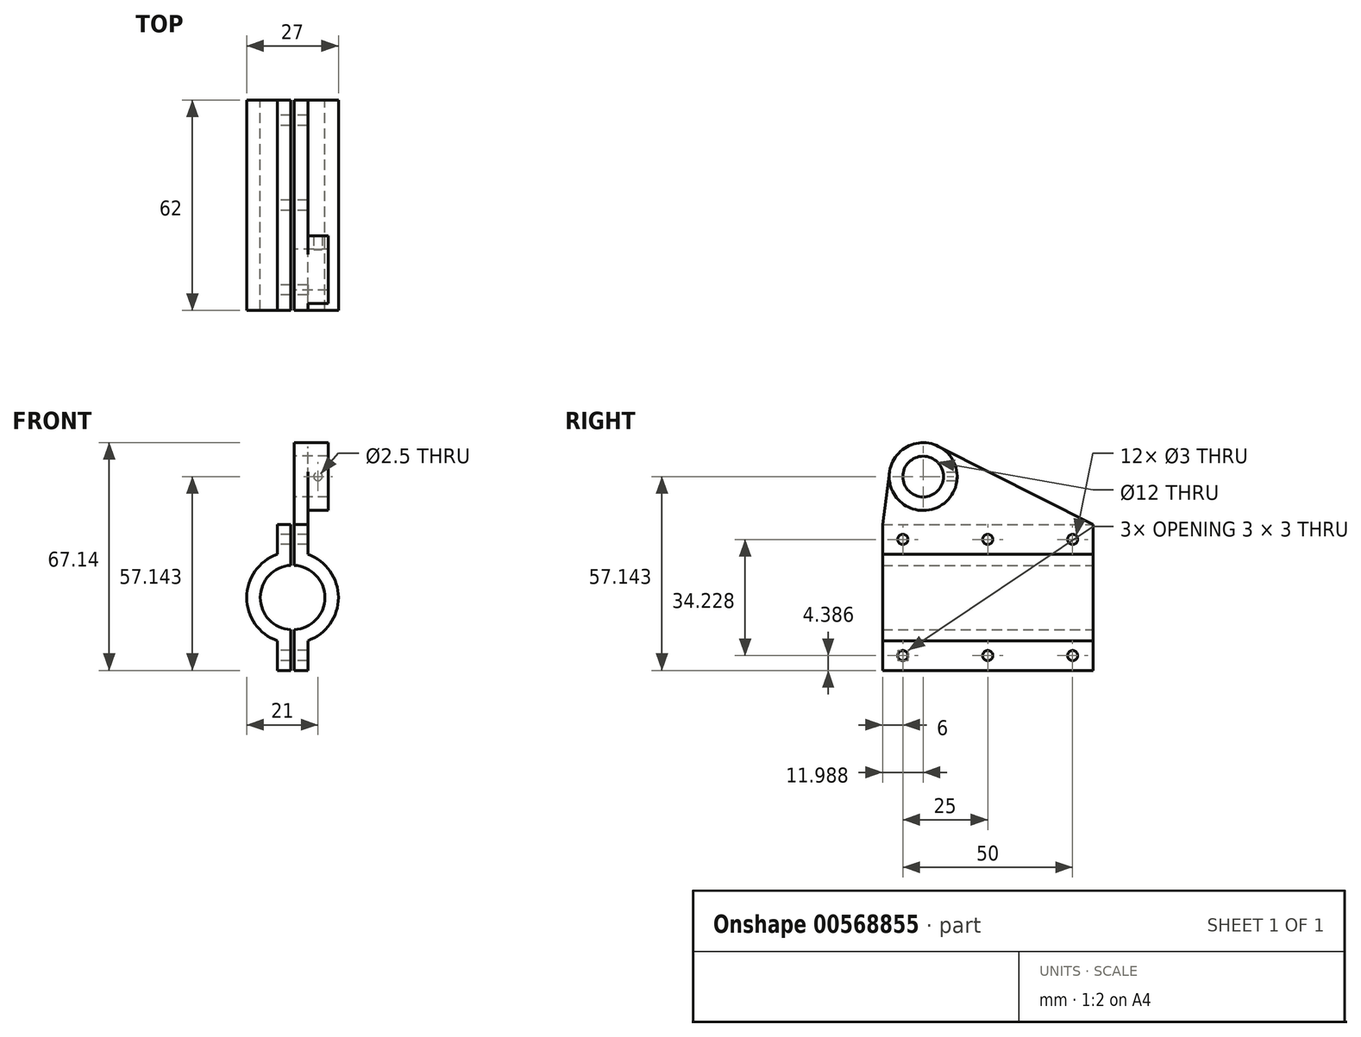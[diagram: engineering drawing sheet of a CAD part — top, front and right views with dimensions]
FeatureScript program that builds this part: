
annotation { "Feature Type Name" : "Feature", "Feature Type Description" : "" }
export const myFeature = defineFeature(function(context is Context, id is Id, definition is map)
    precondition{}
    {
        {
            var Q0;
            Q0=qCreatedBy(makeId("Front.planeOp"),FACE);
            var sketch = newSketch(context, id + "F0", { "sketchPlane" : qUnion([Q0])});
            skArc(sketch, "E0", {"start": v(-0.5, 9.49) * mm, "mid": v(-9.5, 0) * mm, "end": v(-0.5, -9.49) * mm});
            skArc(sketch, "E1", {"start": v(-4.5, 12.73) * mm, "mid": v(-13.5, 0) * mm, "end": v(-4.5, -12.73) * mm});
            skLineSegment(sketch, "E2", {"start": v(0, 28.47) * mm, "end": v(0, -33.23) * mm, "construction": true});
            skCircle(sketch, "E3", {"center": v(0, 0) * mm, "radius": 6 * mm, "construction": true});
            skLineSegment(sketch, "E4", {"start": v(6, 52.38) * mm, "end": v(6, -40.11) * mm, "construction": true});
            skLineSegment(sketch, "E5", {"start": v(-0.5, 21.5) * mm, "end": v(-0.5, 9.49) * mm});
            skLineSegment(sketch, "E6", {"start": v(-0.5, -9.49) * mm, "end": v(-0.5, -21.5) * mm});
            skLineSegment(sketch, "E7", {"start": v(-0.5, 21.5) * mm, "end": v(-4.5, 21.5) * mm});
            skLineSegment(sketch, "E8", {"start": v(-4.5, 21.5) * mm, "end": v(-4.5, 12.73) * mm});
            skLineSegment(sketch, "E9", {"start": v(-0.5, -21.5) * mm, "end": v(-4.5, -21.5) * mm});
            skLineSegment(sketch, "E10", {"start": v(-4.5, -21.5) * mm, "end": v(-4.5, -12.73) * mm});
            skLineSegment(sketch, "E11.MirrorCS", {"start": v(0.5, 21.5) * mm, "end": v(0.5, 9.49) * mm});
            skLineSegment(sketch, "E12.MirrorCS", {"start": v(0.5, 21.5) * mm, "end": v(4.5, 21.5) * mm});
            skLineSegment(sketch, "E13.MirrorCS", {"start": v(4.5, 21.5) * mm, "end": v(4.5, 12.73) * mm});
            skLineSegment(sketch, "E14.MirrorCS", {"start": v(0.5, -9.49) * mm, "end": v(0.5, -21.5) * mm});
            skLineSegment(sketch, "E15.MirrorCS", {"start": v(0.5, -21.5) * mm, "end": v(4.5, -21.5) * mm});
            skLineSegment(sketch, "E16.MirrorCS", {"start": v(4.5, -21.5) * mm, "end": v(4.5, -12.73) * mm});
            skArc(sketch, "E17.trimOffspring", {"start": v(4.5, -12.73) * mm, "mid": v(13.5, 0) * mm, "end": v(4.5, 12.73) * mm});
            skArc(sketch, "E18.trimOffspring", {"start": v(0.5, -9.49) * mm, "mid": v(9.5, 0) * mm, "end": v(0.5, 9.49) * mm});
            skSolve(sketch);
        }
        {
            var Q0;
            Q0 = qSketchRegion(id + "F0", true);
            extrude(context, id + "F1", {"entities" : qUnion([Q0]), "depth" : 62 * mm, "offsetDistance" : 25 * mm});
        }
        {
            var Q0;
            Q0=makeQuery(id+"F1.opExtrude","SWEPT_FACE",FACE,{"disambiguationData":[OSD([sQuery(id+"F0.wireOp",EDGE,"E8")])]});
            var sketch = newSketch(context, id + "F2", { "sketchPlane" : qUnion([Q0])});
            skLineSegment(sketch, "E19.0", {"start": v(62, 21.5) * mm, "end": v(0, 21.5) * mm, "construction": true});
            skLineSegment(sketch, "E19.1", {"start": v(0, 21.5) * mm, "end": v(0, 12.73) * mm, "construction": true});
            skLineSegment(sketch, "E19.2", {"start": v(62, 12.73) * mm, "end": v(0, 12.73) * mm, "construction": true});
            skLineSegment(sketch, "E19.3", {"start": v(62, -12.73) * mm, "end": v(0, -12.73) * mm, "construction": true});
            skLineSegment(sketch, "E19.4", {"start": v(0, -21.5) * mm, "end": v(0, -12.73) * mm, "construction": true});
            skLineSegment(sketch, "E19.5", {"start": v(62, -21.5) * mm, "end": v(0, -21.5) * mm, "construction": true});
            skLineSegment(sketch, "E19.6", {"start": v(62, -21.5) * mm, "end": v(62, -12.73) * mm, "construction": true});
            skLineSegment(sketch, "E19.7", {"start": v(62, 21.5) * mm, "end": v(62, 12.73) * mm, "construction": true});
            skLineSegment(sketch, "E20", {"start": v(0, 17.11) * mm, "end": v(62, 17.11) * mm, "construction": true});
            skLineSegment(sketch, "E21", {"start": v(62, -17.11) * mm, "end": v(0, -17.11) * mm, "construction": true});
            skLineSegment(sketch, "E22", {"start": v(31, -21.5) * mm, "end": v(31, 21.5) * mm, "construction": true});
            skLineSegment(sketch, "E23", {"start": v(6, 21.5) * mm, "end": v(6, -21.5) * mm, "construction": true});
            skLineSegment(sketch, "E24", {"start": v(56, -21.5) * mm, "end": v(56, 21.5) * mm, "construction": true});
            skCircle(sketch, "E25", {"center": v(6, 17.11) * mm, "radius": 1.5 * mm});
            skCircle(sketch, "E26", {"center": v(6, 17.11) * mm, "radius": 1.25 * mm});
            skCircle(sketch, "E27", {"center": v(31, 17.11) * mm, "radius": 1.5 * mm});
            skCircle(sketch, "E28", {"center": v(31, 17.11) * mm, "radius": 1.25 * mm});
            skCircle(sketch, "E29", {"center": v(56, 17.11) * mm, "radius": 1.5 * mm});
            skCircle(sketch, "E30", {"center": v(56, 17.11) * mm, "radius": 1.25 * mm});
            skCircle(sketch, "E31", {"center": v(56, -17.11) * mm, "radius": 1.25 * mm});
            skCircle(sketch, "E32", {"center": v(56, -17.11) * mm, "radius": 1.5 * mm});
            skCircle(sketch, "E33", {"center": v(31, -17.11) * mm, "radius": 1.5 * mm});
            skCircle(sketch, "E34", {"center": v(31, -17.11) * mm, "radius": 1.25 * mm});
            skCircle(sketch, "E35", {"center": v(6, -17.11) * mm, "radius": 1.5 * mm});
            skCircle(sketch, "E36", {"center": v(6, -17.11) * mm, "radius": 1.25 * mm});
            skSolve(sketch);
        }
        {
            var Q0;
            Q0=makeQuery(id+"F2.imprint","IMPRINT",FACE,{"disambiguationData":[TD([[makeQuery(id+"F2.imprint","IMPRINT",EDGE,{"derivedFrom":sQuery(id+"F2.wireOp",EDGE,"E35")}),1.0]])]});
            var Q1;
            Q1=makeQuery(id+"F2.imprint","IMPRINT",FACE,{"disambiguationData":[TD([[makeQuery(id+"F2.imprint","IMPRINT",EDGE,{"derivedFrom":sQuery(id+"F2.wireOp",EDGE,"E36")}),1.0]])]});
            var Q2;
            Q2=makeQuery(id+"F2.imprint","IMPRINT",FACE,{"disambiguationData":[TD([[makeQuery(id+"F2.imprint","IMPRINT",EDGE,{"derivedFrom":sQuery(id+"F2.wireOp",EDGE,"E25")}),1.0]])]});
            var Q3;
            Q3=makeQuery(id+"F2.imprint","IMPRINT",FACE,{"disambiguationData":[TD([[makeQuery(id+"F2.imprint","IMPRINT",EDGE,{"derivedFrom":sQuery(id+"F2.wireOp",EDGE,"E26")}),1.0]])]});
            var Q4;
            Q4=makeQuery(id+"F2.imprint","IMPRINT",FACE,{"disambiguationData":[TD([[makeQuery(id+"F2.imprint","IMPRINT",EDGE,{"derivedFrom":sQuery(id+"F2.wireOp",EDGE,"E27")}),1.0]])]});
            var Q5;
            Q5=makeQuery(id+"F2.imprint","IMPRINT",FACE,{"disambiguationData":[TD([[makeQuery(id+"F2.imprint","IMPRINT",EDGE,{"derivedFrom":sQuery(id+"F2.wireOp",EDGE,"E28")}),1.0]])]});
            var Q6;
            Q6=makeQuery(id+"F2.imprint","IMPRINT",FACE,{"disambiguationData":[TD([[makeQuery(id+"F2.imprint","IMPRINT",EDGE,{"derivedFrom":sQuery(id+"F2.wireOp",EDGE,"E29")}),1.0]])]});
            var Q7;
            Q7=makeQuery(id+"F2.imprint","IMPRINT",FACE,{"disambiguationData":[TD([[makeQuery(id+"F2.imprint","IMPRINT",EDGE,{"derivedFrom":sQuery(id+"F2.wireOp",EDGE,"E30")}),1.0]])]});
            var Q8;
            Q8=makeQuery(id+"F2.imprint","IMPRINT",FACE,{"disambiguationData":[TD([[makeQuery(id+"F2.imprint","IMPRINT",EDGE,{"derivedFrom":sQuery(id+"F2.wireOp",EDGE,"E31")}),-1.0]])]});
            var Q9;
            Q9=makeQuery(id+"F2.imprint","IMPRINT",FACE,{"disambiguationData":[TD([[makeQuery(id+"F2.imprint","IMPRINT",EDGE,{"derivedFrom":sQuery(id+"F2.wireOp",EDGE,"E31")}),1.0]])]});
            var Q10;
            Q10=makeQuery(id+"F2.imprint","IMPRINT",FACE,{"disambiguationData":[TD([[makeQuery(id+"F2.imprint","IMPRINT",EDGE,{"derivedFrom":sQuery(id+"F2.wireOp",EDGE,"E33")}),1.0]])]});
            var Q11;
            Q11=makeQuery(id+"F2.imprint","IMPRINT",FACE,{"disambiguationData":[TD([[makeQuery(id+"F2.imprint","IMPRINT",EDGE,{"derivedFrom":sQuery(id+"F2.wireOp",EDGE,"E34")}),1.0]])]});
            extrude(context, id + "F3", {"entities" : qUnion([Q0, Q1, Q2, Q3, Q4, Q5, Q6, Q7, Q8, Q9, Q10, Q11]), "operationType" : NewBodyOperationType.REMOVE, "oppositeDirection" : true, "depth" : 25 * mm, "offsetDistance" : 25 * mm});
        }
        {
            var Q0;
            Q0=makeQuery(id+"F2.imprint","IMPRINT",FACE,{"disambiguationData":[TD([[makeQuery(id+"F2.imprint","IMPRINT",EDGE,{"derivedFrom":sQuery(id+"F2.wireOp",EDGE,"E26")}),1.0]])]});
            var Q1;
            Q1=makeQuery(id+"F2.imprint","IMPRINT",FACE,{"disambiguationData":[TD([[makeQuery(id+"F2.imprint","IMPRINT",EDGE,{"derivedFrom":sQuery(id+"F2.wireOp",EDGE,"E28")}),1.0]])]});
            var Q2;
            Q2=makeQuery(id+"F2.imprint","IMPRINT",FACE,{"disambiguationData":[TD([[makeQuery(id+"F2.imprint","IMPRINT",EDGE,{"derivedFrom":sQuery(id+"F2.wireOp",EDGE,"E30")}),1.0]])]});
            var Q3;
            Q3=makeQuery(id+"F2.imprint","IMPRINT",FACE,{"disambiguationData":[TD([[makeQuery(id+"F2.imprint","IMPRINT",EDGE,{"derivedFrom":sQuery(id+"F2.wireOp",EDGE,"E31")}),1.0]])]});
            var Q4;
            Q4=makeQuery(id+"F2.imprint","IMPRINT",FACE,{"disambiguationData":[TD([[makeQuery(id+"F2.imprint","IMPRINT",EDGE,{"derivedFrom":sQuery(id+"F2.wireOp",EDGE,"E34")}),1.0]])]});
            var Q5;
            Q5=makeQuery(id+"F2.imprint","IMPRINT",FACE,{"disambiguationData":[TD([[makeQuery(id+"F2.imprint","IMPRINT",EDGE,{"derivedFrom":sQuery(id+"F2.wireOp",EDGE,"E36")}),1.0]])]});
            extrude(context, id + "F4", {"entities" : qUnion([Q0, Q1, Q2, Q3, Q4, Q5]), "operationType" : NewBodyOperationType.REMOVE, "oppositeDirection" : true, "depth" : 25 * mm, "offsetDistance" : 25 * mm});
        }
        {
            var Q0;
            Q0=qCreatedBy(makeId("Right.planeOp"),FACE);
            var sketch = newSketch(context, id + "F5", { "sketchPlane" : qUnion([Q0])});
            skCircle(sketch, "E37", {"center": v(-50.01, 35.64) * mm, "radius": 6 * mm});
            skCircle(sketch, "E38", {"center": v(-50.01, 35.64) * mm, "radius": 10 * mm});
            skLineSegment(sketch, "E39.0", {"start": v(-62, 21.5) * mm, "end": v(0, 21.5) * mm});
            skLineSegment(sketch, "E40", {"start": v(-62, 21.5) * mm, "end": v(-59.92, 36.97) * mm});
            skLineSegment(sketch, "E41", {"start": v(0, 21.5) * mm, "end": v(-45.5, 44.56) * mm});
            skSolve(sketch);
        }
        {
            var Q0;
            Q0=makeQuery(id+"F5.imprint","IMPRINT",FACE,{"disambiguationData":[TD([[makeQuery(id+"F5.imprint","IMPRINT",EDGE,{"derivedFrom":sQuery(id+"F5.wireOp",EDGE,"E39.0")}),1.0]])]});
            var Q1;
            Q1=makeQuery(id+"F1.opExtrude","SWEPT_FACE",FACE,{"disambiguationData":[OSD([sQuery(id+"F0.wireOp",EDGE,"E13.MirrorCS")])]});
            var Q2;
            Q2=makeQuery(id+"F1.opExtrude","SWEPT_FACE",FACE,{"disambiguationData":[OSD([sQuery(id+"F0.wireOp",EDGE,"E11.MirrorCS")])]});
            extrude(context, id + "F6", {"entities" : qUnion([Q0]), "operationType" : NewBodyOperationType.ADD, "endBound" : BoundingType.UP_TO_SURFACE, "depth" : 25 * mm, "endBoundEntityFace" : qUnion([Q1]), "offsetDistance" : 25 * mm, "hasSecondDirection" : true, "secondDirectionBound" : BoundingType.UP_TO_SURFACE, "secondDirectionOppositeDirection" : false, "secondDirectionDepth" : 25 * mm, "secondDirectionBoundEntityFace" : qUnion([Q2])});
        }
        {
            var Q0;
            Q0=makeQuery(id+"F5.imprint","IMPRINT",FACE,{"disambiguationData":[TD([[makeQuery(id+"F5.imprint","IMPRINT",EDGE,{"derivedFrom":sQuery(id+"F5.wireOp",EDGE,"E37")}),-1.0]])]});
            var Q1;
            {var subQ0=sQuery(id+"F0.wireOp",EDGE,"E13.MirrorCS");Q1=makeQuery(id+"F6.boolean.opBoolean","MERGE",FACE,{"derivedFrom":[makeQuery(id+"F1.opExtrude","SWEPT_FACE",FACE,{"disambiguationData":[OSD([subQ0])]}),makeQuery(id+"F6.opExtrude","CAP_FACE",FACE,{"disambiguationData":[OSD([subQ0])],"isStart":false})]});}
            var Q2;
            {var subQ0=sQuery(id+"F0.wireOp",EDGE,"E11.MirrorCS");Q2=makeQuery(id+"F6.boolean.opBoolean","MERGE",FACE,{"derivedFrom":[makeQuery(id+"F1.opExtrude","SWEPT_FACE",FACE,{"disambiguationData":[OSD([subQ0])]}),makeQuery(id+"F6.opExtrude","CAP_FACE",FACE,{"disambiguationData":[OSD([subQ0])],"isStart":true})]});}
            extrude(context, id + "F7", {"entities" : qUnion([Q0]), "operationType" : NewBodyOperationType.ADD, "endBound" : BoundingType.UP_TO_SURFACE, "depth" : 25 * mm, "endBoundEntityFace" : qUnion([Q1]), "hasOffset" : true, "offsetDistance" : 6 * mm, "offsetOppositeDirection" : true, "hasSecondDirection" : true, "secondDirectionBound" : BoundingType.UP_TO_SURFACE, "secondDirectionOppositeDirection" : false, "secondDirectionDepth" : 25 * mm, "secondDirectionBoundEntityFace" : qUnion([Q2])});
        }
        {
            var Q0;
            Q0=qCreatedBy(makeId("Front.planeOp"),FACE);
            var Q1;
            Q1=sQuery(id+"F5.wireOp",VERTEX,"E37.center");
            cPlane(context, id + "F8", {"entities" : qUnion([Q0, Q1]), "cplaneType" : CPlaneType.PLANE_POINT, "offset" : 25 * mm, "width" : 150 * mm, "height" : 150 * mm});
        }
        {
            var Q0;
            Q0=qCreatedBy(id+"F8.planeOp",FACE);
            var sketch = newSketch(context, id + "F9", { "sketchPlane" : qUnion([Q0])});
            skPoint(sketch, "E42.0", {"position": v(0, 35.64) * mm});
            skLineSegment(sketch, "E43.0", {"start": v(10.5, 45.64) * mm, "end": v(10.5, 25.64) * mm, "construction": true});
            skLineSegment(sketch, "E43.1", {"start": v(4.5, 25.64) * mm, "end": v(4.5, 44.56) * mm, "construction": true});
            skLineSegment(sketch, "E44", {"start": v(4.5, 35.64) * mm, "end": v(10.5, 35.64) * mm, "construction": true});
            skCircle(sketch, "E45", {"center": v(7.5, 35.64) * mm, "radius": 1.25 * mm});
            skSolve(sketch);
        }
        {
            var Q0;
            Q0=makeQuery(id+"F9.imprint","IMPRINT",FACE,{"disambiguationData":[TD([[makeQuery(id+"F9.imprint","IMPRINT",EDGE,{"derivedFrom":sQuery(id+"F9.wireOp",EDGE,"E45")}),1.0]])]});
            extrude(context, id + "F10", {"entities" : qUnion([Q0]), "operationType" : NewBodyOperationType.REMOVE, "oppositeDirection" : true, "depth" : 25 * mm, "offsetDistance" : 25 * mm});
        }
    });
